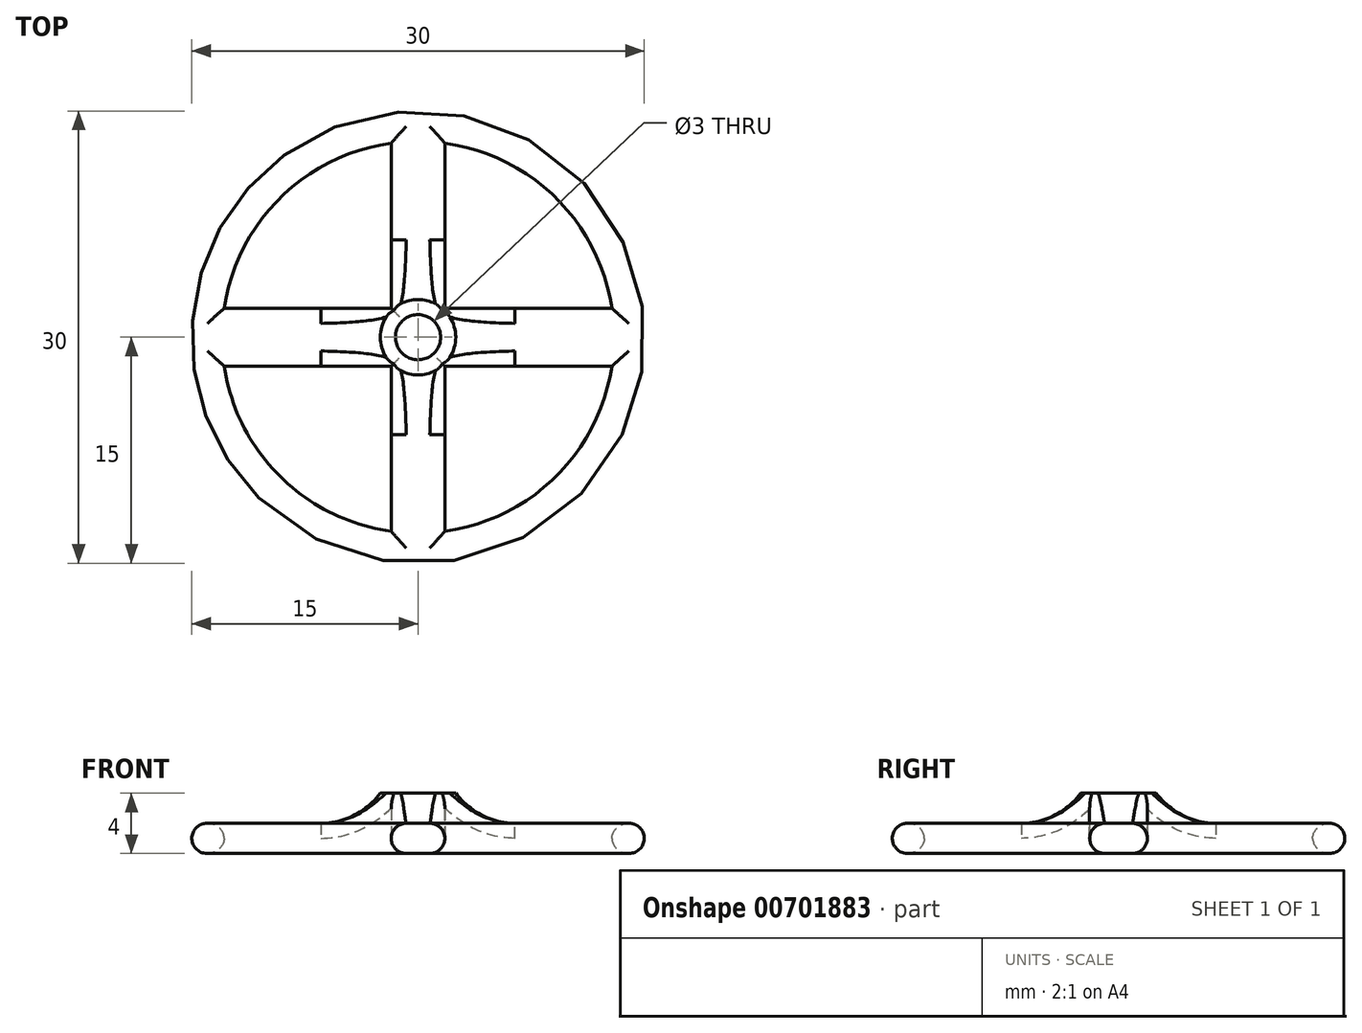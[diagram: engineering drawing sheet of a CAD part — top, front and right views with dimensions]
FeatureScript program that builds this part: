
annotation { "Feature Type Name" : "Feature", "Feature Type Description" : "" }
export const myFeature = defineFeature(function(context is Context, id is Id, definition is map)
    precondition{}
    {
        {
            var Q0;
            Q0=qCreatedBy(makeId("Top.planeOp"),FACE);
            var sketch = newSketch(context, id + "F0", { "sketchPlane" : qUnion([Q0])});
            skCircle(sketch, "E0", {"center": v(0, 0) * mm, "radius": 15 * mm});
            skLineSegment(sketch, "E1.bottom", {"start": v(1.78, -14.9) * mm, "end": v(-1.78, -14.9) * mm});
            skLineSegment(sketch, "E1.top", {"start": v(1.78, 14.9) * mm, "end": v(-1.78, 14.9) * mm});
            skLineSegment(sketch, "E1.left", {"start": v(1.78, -14.9) * mm, "end": v(1.78, 14.9) * mm});
            skLineSegment(sketch, "E1.right", {"start": v(-1.78, -14.9) * mm, "end": v(-1.78, 14.9) * mm});
            skLineSegment(sketch, "E2.bottom", {"start": v(14.88, -1.91) * mm, "end": v(-14.88, -1.91) * mm});
            skLineSegment(sketch, "E2.top", {"start": v(14.88, 1.91) * mm, "end": v(-14.88, 1.91) * mm});
            skLineSegment(sketch, "E2.left", {"start": v(14.88, -1.91) * mm, "end": v(14.88, 1.91) * mm});
            skLineSegment(sketch, "E2.right", {"start": v(-14.88, -1.91) * mm, "end": v(-14.88, 1.91) * mm});
            skCircle(sketch, "E3", {"center": v(0, 0) * mm, "radius": 1.57 * mm});
            skCircle(sketch, "E4", {"center": v(0, 0) * mm, "radius": 13 * mm});
            skSolve(sketch);
        }
        {
            var Q0;
            {var subQ0=sQuery(id+"F0.wireOp",EDGE,"E2.right");Q0=makeQuery(id+"F0.imprint","IMPRINT",FACE,{"disambiguationData":[TD([[makeQuery(id+"F0.imprint","IMPRINT",EDGE,{"derivedFrom":subQ0}),1.0]])]});}
            var Q1;
            {var subQ0=sQuery(id+"F0.wireOp",EDGE,"E2.right");Q1=makeQuery(id+"F0.imprint","IMPRINT",FACE,{"disambiguationData":[TD([[makeQuery(id+"F0.imprint","IMPRINT",EDGE,{"derivedFrom":subQ0}),-1.0]])]});}
            var Q2;
            {var subQ0=sQuery(id+"F0.wireOp",EDGE,"E1.right");var subQ5=sQuery(id+"F0.wireOp",EDGE,"E4");var subQ6=makeQuery(id+"F0.imprint","INTERSECT",VERTEX,{"disambiguationData":[OD(1.0)],"derivedFrom":[subQ0,subQ5]});Q2=makeQuery(id+"F0.imprint","IMPRINT",FACE,{"disambiguationData":[TD([[makeQuery(id+"F0.imprint","IMPRINT",EDGE,{"disambiguationData":[TD([[subQ6,-1.0]])],"derivedFrom":subQ5}),-1.0]])]});}
            var Q3;
            {var subQ0=sQuery(id+"F0.wireOp",EDGE,"E1.top");Q3=makeQuery(id+"F0.imprint","IMPRINT",FACE,{"disambiguationData":[TD([[makeQuery(id+"F0.imprint","IMPRINT",EDGE,{"derivedFrom":subQ0}),1.0]])]});}
            var Q4;
            {var subQ0=sQuery(id+"F0.wireOp",EDGE,"E1.top");Q4=makeQuery(id+"F0.imprint","IMPRINT",FACE,{"disambiguationData":[TD([[makeQuery(id+"F0.imprint","IMPRINT",EDGE,{"derivedFrom":subQ0}),-1.0]])]});}
            var Q5;
            {var subQ0=sQuery(id+"F0.wireOp",EDGE,"E2.left");Q5=makeQuery(id+"F0.imprint","IMPRINT",FACE,{"disambiguationData":[TD([[makeQuery(id+"F0.imprint","IMPRINT",EDGE,{"derivedFrom":subQ0}),-1.0]])]});}
            var Q6;
            {var subQ0=sQuery(id+"F0.wireOp",EDGE,"E2.left");Q6=makeQuery(id+"F0.imprint","IMPRINT",FACE,{"disambiguationData":[TD([[makeQuery(id+"F0.imprint","IMPRINT",EDGE,{"derivedFrom":subQ0}),1.0]])]});}
            var Q7;
            {var subQ0=sQuery(id+"F0.wireOp",EDGE,"E1.left");var subQ5=sQuery(id+"F0.wireOp",EDGE,"E4");var subQ7=makeQuery(id+"F0.imprint","INTERSECT",VERTEX,{"disambiguationData":[OD(1.0)],"derivedFrom":[subQ0,subQ5]});Q7=makeQuery(id+"F0.imprint","IMPRINT",FACE,{"disambiguationData":[TD([[makeQuery(id+"F0.imprint","IMPRINT",EDGE,{"disambiguationData":[TD([[subQ7,1.0]])],"derivedFrom":subQ5}),-1.0]])]});}
            var Q8;
            {var subQ0=sQuery(id+"F0.wireOp",EDGE,"E2.top");var subQ1=sQuery(id+"F0.wireOp",EDGE,"E1.left");var subQ2=makeQuery(id+"F0.imprint","INTERSECT",VERTEX,{"derivedFrom":[subQ1,subQ0]});Q8=makeQuery(id+"F0.imprint","IMPRINT",FACE,{"disambiguationData":[TD([[makeQuery(id+"F0.imprint","IMPRINT",EDGE,{"disambiguationData":[TD([[subQ2,-1.0]])],"derivedFrom":subQ1}),1.0]])]});}
            var Q9;
            Q9=makeQuery(id+"F0.imprint","IMPRINT",FACE,{"disambiguationData":[TD([[makeQuery(id+"F0.imprint","IMPRINT",EDGE,{"derivedFrom":sQuery(id+"F0.wireOp",EDGE,"E3")}),-1.0]])]});
            var Q10;
            {var subQ0=sQuery(id+"F0.wireOp",EDGE,"E2.bottom");var subQ1=sQuery(id+"F0.wireOp",EDGE,"E1.left");var subQ2=makeQuery(id+"F0.imprint","INTERSECT",VERTEX,{"derivedFrom":[subQ1,subQ0]});Q10=makeQuery(id+"F0.imprint","IMPRINT",FACE,{"disambiguationData":[TD([[makeQuery(id+"F0.imprint","IMPRINT",EDGE,{"disambiguationData":[TD([[subQ2,-1.0]])],"derivedFrom":subQ1}),-1.0]])]});}
            var Q11;
            {var subQ0=sQuery(id+"F0.wireOp",EDGE,"E2.bottom");var subQ1=sQuery(id+"F0.wireOp",EDGE,"E1.right");var subQ2=makeQuery(id+"F0.imprint","INTERSECT",VERTEX,{"derivedFrom":[subQ1,subQ0]});Q11=makeQuery(id+"F0.imprint","IMPRINT",FACE,{"disambiguationData":[TD([[makeQuery(id+"F0.imprint","IMPRINT",EDGE,{"disambiguationData":[TD([[subQ2,-1.0]])],"derivedFrom":subQ1}),1.0]])]});}
            var Q12;
            {var subQ0=sQuery(id+"F0.wireOp",EDGE,"E4");var subQ1=sQuery(id+"F0.wireOp",EDGE,"E1.left");var subQ2=makeQuery(id+"F0.imprint","INTERSECT",VERTEX,{"disambiguationData":[OD(0.0)],"derivedFrom":[subQ1,subQ0]});Q12=makeQuery(id+"F0.imprint","IMPRINT",FACE,{"disambiguationData":[TD([[makeQuery(id+"F0.imprint","IMPRINT",EDGE,{"disambiguationData":[TD([[subQ2,-1.0]])],"derivedFrom":subQ1}),1.0]])]});}
            var Q13;
            {var subQ0=sQuery(id+"F0.wireOp",EDGE,"E1.right");var subQ5=sQuery(id+"F0.wireOp",EDGE,"E4");var subQ7=makeQuery(id+"F0.imprint","INTERSECT",VERTEX,{"disambiguationData":[OD(0.0)],"derivedFrom":[subQ0,subQ5]});Q13=makeQuery(id+"F0.imprint","IMPRINT",FACE,{"disambiguationData":[TD([[makeQuery(id+"F0.imprint","IMPRINT",EDGE,{"disambiguationData":[TD([[subQ7,1.0]])],"derivedFrom":subQ5}),-1.0]])]});}
            var Q14;
            {var subQ0=sQuery(id+"F0.wireOp",EDGE,"E1.bottom");Q14=makeQuery(id+"F0.imprint","IMPRINT",FACE,{"disambiguationData":[TD([[makeQuery(id+"F0.imprint","IMPRINT",EDGE,{"derivedFrom":subQ0}),-1.0]])]});}
            var Q15;
            {var subQ0=sQuery(id+"F0.wireOp",EDGE,"E1.bottom");Q15=makeQuery(id+"F0.imprint","IMPRINT",FACE,{"disambiguationData":[TD([[makeQuery(id+"F0.imprint","IMPRINT",EDGE,{"derivedFrom":subQ0}),1.0]])]});}
            var Q16;
            {var subQ0=sQuery(id+"F0.wireOp",EDGE,"E1.left");var subQ5=sQuery(id+"F0.wireOp",EDGE,"E4");var subQ6=makeQuery(id+"F0.imprint","INTERSECT",VERTEX,{"disambiguationData":[OD(0.0)],"derivedFrom":[subQ0,subQ5]});Q16=makeQuery(id+"F0.imprint","IMPRINT",FACE,{"disambiguationData":[TD([[makeQuery(id+"F0.imprint","IMPRINT",EDGE,{"disambiguationData":[TD([[subQ6,-1.0]])],"derivedFrom":subQ5}),-1.0]])]});}
            extrude(context, id + "F1", {"entities" : qUnion([Q0, Q1, Q2, Q3, Q4, Q5, Q6, Q7, Q8, Q9, Q10, Q11, Q12, Q13, Q14, Q15, Q16]), "depth" : 2 * mm, "offsetDistance" : 25 * mm});
        }
        {
            var Q0;
            Q0=qCreatedBy(makeId("Top.planeOp"),FACE);
            var sketch = newSketch(context, id + "F2", { "sketchPlane" : qUnion([Q0])});
            skCircle(sketch, "E5", {"center": v(0, 0) * mm, "radius": 2.5 * mm});
            skSolve(sketch);
        }
        {
            var Q0;
            Q0=makeQuery(id+"F2.imprint","IMPRINT",FACE,{"disambiguationData":[TD([[makeQuery(id+"F2.imprint","IMPRINT",EDGE,{"derivedFrom":sQuery(id+"F2.wireOp",EDGE,"E5")}),1.0]])]});
            extrude(context, id + "F3", {"entities" : qUnion([Q0]), "operationType" : NewBodyOperationType.ADD, "depth" : 4 * mm, "offsetDistance" : 25 * mm});
        }
        {
            var Q0;
            Q0=qCreatedBy(makeId("Top.planeOp"),FACE);
            var sketch = newSketch(context, id + "F4", { "sketchPlane" : qUnion([Q0])});
            skCircle(sketch, "E6", {"center": v(0, 0) * mm, "radius": 1.5 * mm});
            skSolve(sketch);
        }
        {
            var Q0;
            Q0=makeQuery(id+"F4.imprint","IMPRINT",FACE,{"disambiguationData":[TD([[makeQuery(id+"F4.imprint","IMPRINT",EDGE,{"derivedFrom":sQuery(id+"F4.wireOp",EDGE,"E6")}),1.0]])]});
            extrude(context, id + "F5", {"entities" : qUnion([Q0]), "operationType" : NewBodyOperationType.REMOVE, "depth" : 5 * mm, "offsetDistance" : 25 * mm});
        }
        {
            var Q0;
            Q0=makeQuery(id+"F1.opExtrude","CAP_EDGE",EDGE,{"disambiguationData":[OSD([sQuery(id+"F0.wireOp",EDGE,"E0")])],"isStart":false});
            fillet(context, id + "F6", {"entities" : qUnion([Q0]), "tangentPropagation" : true, "radius" : 1 * mm, "defaultsChanged" : true, "vertexSettings" : [], "allowEdgeOverflow" : false});
        }
        {
            var Q0;
            Q0=makeQuery(id+"F1.opExtrude","CAP_EDGE",EDGE,{"disambiguationData":[OSD([sQuery(id+"F0.wireOp",EDGE,"E0")])],"isStart":true});
            fillet(context, id + "F7", {"entities" : qUnion([Q0]), "tangentPropagation" : true, "radius" : 1 * mm, "defaultsChanged" : true, "vertexSettings" : [], "allowEdgeOverflow" : false});
        }
        {
            var Q0;
            Q0=makeQuery(id+"F3.boolean.opBoolean","INTERSECT",EDGE,{"derivedFrom":[makeQuery(id+"F1.opExtrude","CAP_FACE",FACE,{"disambiguationData":[OSD([sQuery(id+"F0.wireOp",EDGE,"E0"),sQuery(id+"F0.wireOp",EDGE,"E1.left"),sQuery(id+"F0.wireOp",EDGE,"E1.right"),sQuery(id+"F0.wireOp",EDGE,"E2.bottom"),sQuery(id+"F0.wireOp",EDGE,"E2.top"),sQuery(id+"F0.wireOp",EDGE,"E3"),sQuery(id+"F0.wireOp",EDGE,"E4")])],"isStart":false}),makeQuery(id+"F3.opExtrude","SWEPT_FACE",FACE,{"disambiguationData":[OSD([sQuery(id+"F2.wireOp",EDGE,"E5")])]})]});
            fillet(context, id + "F8", {"entities" : qUnion([Q0]), "tangentPropagation" : true, "radius" : 5 * mm, "defaultsChanged" : false, "vertexSettings" : [], "allowEdgeOverflow" : false});
        }
        {
            var Q0;
            {var subQ0=sQuery(id+"F0.wireOp",EDGE,"E1.right");Q0=makeQuery(id+"F1.opExtrude","CAP_EDGE",EDGE,{"disambiguationData":[OSD([subQ0]),TDD([makeQuery(id+"F0.imprint","IMPRINT",EDGE,{"disambiguationData":[TD([[makeQuery(id+"F0.imprint","INTERSECT",VERTEX,{"disambiguationData":[OD(0.0)],"derivedFrom":[subQ0,sQuery(id+"F0.wireOp",EDGE,"E4")]}),-1.0]])],"derivedFrom":subQ0})])],"isStart":true});}
            var Q1;
            {var subQ0=sQuery(id+"F0.wireOp",EDGE,"E1.left");Q1=makeQuery(id+"F1.opExtrude","CAP_EDGE",EDGE,{"disambiguationData":[OSD([subQ0]),TDD([makeQuery(id+"F0.imprint","IMPRINT",EDGE,{"disambiguationData":[TD([[makeQuery(id+"F0.imprint","INTERSECT",VERTEX,{"disambiguationData":[OD(0.0)],"derivedFrom":[subQ0,sQuery(id+"F0.wireOp",EDGE,"E4")]}),-1.0]])],"derivedFrom":subQ0})])],"isStart":true});}
            var Q2;
            {var subQ0=sQuery(id+"F0.wireOp",EDGE,"E1.left");Q2=makeQuery(id+"F1.opExtrude","CAP_EDGE",EDGE,{"disambiguationData":[OSD([subQ0]),TDD([makeQuery(id+"F0.imprint","IMPRINT",EDGE,{"disambiguationData":[TD([[makeQuery(id+"F0.imprint","INTERSECT",VERTEX,{"derivedFrom":[subQ0,sQuery(id+"F0.wireOp",EDGE,"E2.top")]}),-1.0]])],"derivedFrom":subQ0})])],"isStart":true});}
            var Q3;
            {var subQ0=sQuery(id+"F0.wireOp",EDGE,"E1.right");Q3=makeQuery(id+"F1.opExtrude","CAP_EDGE",EDGE,{"disambiguationData":[OSD([subQ0]),TDD([makeQuery(id+"F0.imprint","IMPRINT",EDGE,{"disambiguationData":[TD([[makeQuery(id+"F0.imprint","INTERSECT",VERTEX,{"derivedFrom":[subQ0,sQuery(id+"F0.wireOp",EDGE,"E2.top")]}),-1.0]])],"derivedFrom":subQ0})])],"isStart":true});}
            var Q4;
            {var subQ0=sQuery(id+"F0.wireOp",EDGE,"E2.bottom");Q4=makeQuery(id+"F1.opExtrude","CAP_EDGE",EDGE,{"disambiguationData":[OSD([subQ0]),TDD([makeQuery(id+"F0.imprint","IMPRINT",EDGE,{"disambiguationData":[TD([[makeQuery(id+"F0.imprint","INTERSECT",VERTEX,{"derivedFrom":[sQuery(id+"F0.wireOp",EDGE,"E1.right"),subQ0]}),-1.0]])],"derivedFrom":subQ0})])],"isStart":true});}
            var Q5;
            {var subQ0=sQuery(id+"F0.wireOp",EDGE,"E2.top");Q5=makeQuery(id+"F1.opExtrude","CAP_EDGE",EDGE,{"disambiguationData":[OSD([subQ0]),TDD([makeQuery(id+"F0.imprint","IMPRINT",EDGE,{"disambiguationData":[TD([[makeQuery(id+"F0.imprint","INTERSECT",VERTEX,{"derivedFrom":[sQuery(id+"F0.wireOp",EDGE,"E1.right"),subQ0]}),-1.0]])],"derivedFrom":subQ0})])],"isStart":true});}
            var Q6;
            {var subQ0=sQuery(id+"F0.wireOp",EDGE,"E2.top");Q6=makeQuery(id+"F1.opExtrude","CAP_EDGE",EDGE,{"disambiguationData":[OSD([subQ0]),TDD([makeQuery(id+"F0.imprint","IMPRINT",EDGE,{"disambiguationData":[TD([[makeQuery(id+"F0.imprint","INTERSECT",VERTEX,{"derivedFrom":[sQuery(id+"F0.wireOp",EDGE,"E1.left"),subQ0]}),1.0]])],"derivedFrom":subQ0})])],"isStart":true});}
            var Q7;
            {var subQ0=sQuery(id+"F0.wireOp",EDGE,"E2.bottom");Q7=makeQuery(id+"F1.opExtrude","CAP_EDGE",EDGE,{"disambiguationData":[OSD([subQ0]),TDD([makeQuery(id+"F0.imprint","IMPRINT",EDGE,{"disambiguationData":[TD([[makeQuery(id+"F0.imprint","INTERSECT",VERTEX,{"derivedFrom":[sQuery(id+"F0.wireOp",EDGE,"E1.left"),subQ0]}),1.0]])],"derivedFrom":subQ0})])],"isStart":true});}
            var Q8;
            {var subQ0=sQuery(id+"F0.wireOp",EDGE,"E4");Q8=makeQuery(id+"F1.opExtrude","CAP_EDGE",EDGE,{"disambiguationData":[OSD([subQ0]),TDD([makeQuery(id+"F0.imprint","IMPRINT",EDGE,{"disambiguationData":[TD([[makeQuery(id+"F0.imprint","INTERSECT",VERTEX,{"disambiguationData":[OD(1.0)],"derivedFrom":[sQuery(id+"F0.wireOp",EDGE,"E1.right"),subQ0]}),-1.0]])],"derivedFrom":subQ0})])],"isStart":true});}
            var Q9;
            {var subQ0=sQuery(id+"F0.wireOp",EDGE,"E4");Q9=makeQuery(id+"F1.opExtrude","CAP_EDGE",EDGE,{"disambiguationData":[OSD([subQ0]),TDD([makeQuery(id+"F0.imprint","IMPRINT",EDGE,{"disambiguationData":[TD([[makeQuery(id+"F0.imprint","INTERSECT",VERTEX,{"disambiguationData":[OD(1.0)],"derivedFrom":[sQuery(id+"F0.wireOp",EDGE,"E1.left"),subQ0]}),1.0]])],"derivedFrom":subQ0})])],"isStart":true});}
            var Q10;
            {var subQ0=sQuery(id+"F0.wireOp",EDGE,"E4");Q10=makeQuery(id+"F1.opExtrude","CAP_EDGE",EDGE,{"disambiguationData":[OSD([subQ0]),TDD([makeQuery(id+"F0.imprint","IMPRINT",EDGE,{"disambiguationData":[TD([[makeQuery(id+"F0.imprint","INTERSECT",VERTEX,{"disambiguationData":[OD(0.0)],"derivedFrom":[sQuery(id+"F0.wireOp",EDGE,"E1.right"),subQ0]}),1.0]])],"derivedFrom":subQ0})])],"isStart":true});}
            var Q11;
            {var subQ0=sQuery(id+"F0.wireOp",EDGE,"E4");Q11=makeQuery(id+"F1.opExtrude","CAP_EDGE",EDGE,{"disambiguationData":[OSD([subQ0]),TDD([makeQuery(id+"F0.imprint","IMPRINT",EDGE,{"disambiguationData":[TD([[makeQuery(id+"F0.imprint","INTERSECT",VERTEX,{"disambiguationData":[OD(0.0)],"derivedFrom":[sQuery(id+"F0.wireOp",EDGE,"E1.left"),subQ0]}),-1.0]])],"derivedFrom":subQ0})])],"isStart":true});}
            var Q12;
            {var subQ0=sQuery(id+"F0.wireOp",EDGE,"E4");Q12=makeQuery(id+"F1.opExtrude","CAP_EDGE",EDGE,{"disambiguationData":[OSD([subQ0]),TDD([makeQuery(id+"F0.imprint","IMPRINT",EDGE,{"disambiguationData":[TD([[makeQuery(id+"F0.imprint","INTERSECT",VERTEX,{"disambiguationData":[OD(1.0)],"derivedFrom":[sQuery(id+"F0.wireOp",EDGE,"E1.right"),subQ0]}),-1.0]])],"derivedFrom":subQ0})])],"isStart":false});}
            var Q13;
            {var subQ0=sQuery(id+"F0.wireOp",EDGE,"E4");Q13=makeQuery(id+"F1.opExtrude","CAP_EDGE",EDGE,{"disambiguationData":[OSD([subQ0]),TDD([makeQuery(id+"F0.imprint","IMPRINT",EDGE,{"disambiguationData":[TD([[makeQuery(id+"F0.imprint","INTERSECT",VERTEX,{"disambiguationData":[OD(1.0)],"derivedFrom":[sQuery(id+"F0.wireOp",EDGE,"E1.left"),subQ0]}),1.0]])],"derivedFrom":subQ0})])],"isStart":false});}
            var Q14;
            {var subQ0=sQuery(id+"F0.wireOp",EDGE,"E4");Q14=makeQuery(id+"F1.opExtrude","CAP_EDGE",EDGE,{"disambiguationData":[OSD([subQ0]),TDD([makeQuery(id+"F0.imprint","IMPRINT",EDGE,{"disambiguationData":[TD([[makeQuery(id+"F0.imprint","INTERSECT",VERTEX,{"disambiguationData":[OD(0.0)],"derivedFrom":[sQuery(id+"F0.wireOp",EDGE,"E1.left"),subQ0]}),-1.0]])],"derivedFrom":subQ0})])],"isStart":false});}
            var Q15;
            {var subQ0=sQuery(id+"F0.wireOp",EDGE,"E4");Q15=makeQuery(id+"F1.opExtrude","CAP_EDGE",EDGE,{"disambiguationData":[OSD([subQ0]),TDD([makeQuery(id+"F0.imprint","IMPRINT",EDGE,{"disambiguationData":[TD([[makeQuery(id+"F0.imprint","INTERSECT",VERTEX,{"disambiguationData":[OD(0.0)],"derivedFrom":[sQuery(id+"F0.wireOp",EDGE,"E1.right"),subQ0]}),1.0]])],"derivedFrom":subQ0})])],"isStart":false});}
            var Q16;
            {var subQ0=sQuery(id+"F0.wireOp",EDGE,"E2.bottom");Q16=makeQuery(id+"F1.opExtrude","CAP_EDGE",EDGE,{"disambiguationData":[OSD([subQ0]),TDD([makeQuery(id+"F0.imprint","IMPRINT",EDGE,{"disambiguationData":[TD([[makeQuery(id+"F0.imprint","INTERSECT",VERTEX,{"derivedFrom":[sQuery(id+"F0.wireOp",EDGE,"E1.left"),subQ0]}),1.0]])],"derivedFrom":subQ0})])],"isStart":false});}
            var Q17;
            {var subQ0=sQuery(id+"F0.wireOp",EDGE,"E2.top");Q17=makeQuery(id+"F1.opExtrude","CAP_EDGE",EDGE,{"disambiguationData":[OSD([subQ0]),TDD([makeQuery(id+"F0.imprint","IMPRINT",EDGE,{"disambiguationData":[TD([[makeQuery(id+"F0.imprint","INTERSECT",VERTEX,{"derivedFrom":[sQuery(id+"F0.wireOp",EDGE,"E1.left"),subQ0]}),1.0]])],"derivedFrom":subQ0})])],"isStart":false});}
            var Q18;
            {var subQ0=sQuery(id+"F0.wireOp",EDGE,"E1.left");Q18=makeQuery(id+"F1.opExtrude","CAP_EDGE",EDGE,{"disambiguationData":[OSD([subQ0]),TDD([makeQuery(id+"F0.imprint","IMPRINT",EDGE,{"disambiguationData":[TD([[makeQuery(id+"F0.imprint","INTERSECT",VERTEX,{"derivedFrom":[subQ0,sQuery(id+"F0.wireOp",EDGE,"E2.top")]}),-1.0]])],"derivedFrom":subQ0})])],"isStart":false});}
            var Q19;
            {var subQ0=sQuery(id+"F0.wireOp",EDGE,"E1.right");Q19=makeQuery(id+"F1.opExtrude","CAP_EDGE",EDGE,{"disambiguationData":[OSD([subQ0]),TDD([makeQuery(id+"F0.imprint","IMPRINT",EDGE,{"disambiguationData":[TD([[makeQuery(id+"F0.imprint","INTERSECT",VERTEX,{"derivedFrom":[subQ0,sQuery(id+"F0.wireOp",EDGE,"E2.top")]}),-1.0]])],"derivedFrom":subQ0})])],"isStart":false});}
            var Q20;
            {var subQ0=sQuery(id+"F0.wireOp",EDGE,"E2.bottom");Q20=makeQuery(id+"F1.opExtrude","CAP_EDGE",EDGE,{"disambiguationData":[OSD([subQ0]),TDD([makeQuery(id+"F0.imprint","IMPRINT",EDGE,{"disambiguationData":[TD([[makeQuery(id+"F0.imprint","INTERSECT",VERTEX,{"derivedFrom":[sQuery(id+"F0.wireOp",EDGE,"E1.right"),subQ0]}),-1.0]])],"derivedFrom":subQ0})])],"isStart":false});}
            var Q21;
            {var subQ0=sQuery(id+"F0.wireOp",EDGE,"E2.top");Q21=makeQuery(id+"F1.opExtrude","CAP_EDGE",EDGE,{"disambiguationData":[OSD([subQ0]),TDD([makeQuery(id+"F0.imprint","IMPRINT",EDGE,{"disambiguationData":[TD([[makeQuery(id+"F0.imprint","INTERSECT",VERTEX,{"derivedFrom":[sQuery(id+"F0.wireOp",EDGE,"E1.right"),subQ0]}),-1.0]])],"derivedFrom":subQ0})])],"isStart":false});}
            var Q22;
            {var subQ0=sQuery(id+"F0.wireOp",EDGE,"E1.right");Q22=makeQuery(id+"F1.opExtrude","CAP_EDGE",EDGE,{"disambiguationData":[OSD([subQ0]),TDD([makeQuery(id+"F0.imprint","IMPRINT",EDGE,{"disambiguationData":[TD([[makeQuery(id+"F0.imprint","INTERSECT",VERTEX,{"disambiguationData":[OD(0.0)],"derivedFrom":[subQ0,sQuery(id+"F0.wireOp",EDGE,"E4")]}),-1.0]])],"derivedFrom":subQ0})])],"isStart":false});}
            var Q23;
            {var subQ0=sQuery(id+"F0.wireOp",EDGE,"E1.left");Q23=makeQuery(id+"F1.opExtrude","CAP_EDGE",EDGE,{"disambiguationData":[OSD([subQ0]),TDD([makeQuery(id+"F0.imprint","IMPRINT",EDGE,{"disambiguationData":[TD([[makeQuery(id+"F0.imprint","INTERSECT",VERTEX,{"disambiguationData":[OD(0.0)],"derivedFrom":[subQ0,sQuery(id+"F0.wireOp",EDGE,"E4")]}),-1.0]])],"derivedFrom":subQ0})])],"isStart":false});}
            fillet(context, id + "F9", {"entities" : qUnion([Q0, Q1, Q2, Q3, Q4, Q5, Q6, Q7, Q8, Q9, Q10, Q11, Q12, Q13, Q14, Q15, Q16, Q17, Q18, Q19, Q20, Q21, Q22, Q23]), "tangentPropagation" : true, "radius" : 1 * mm, "defaultsChanged" : false, "vertexSettings" : [], "allowEdgeOverflow" : false});
        }
    });
